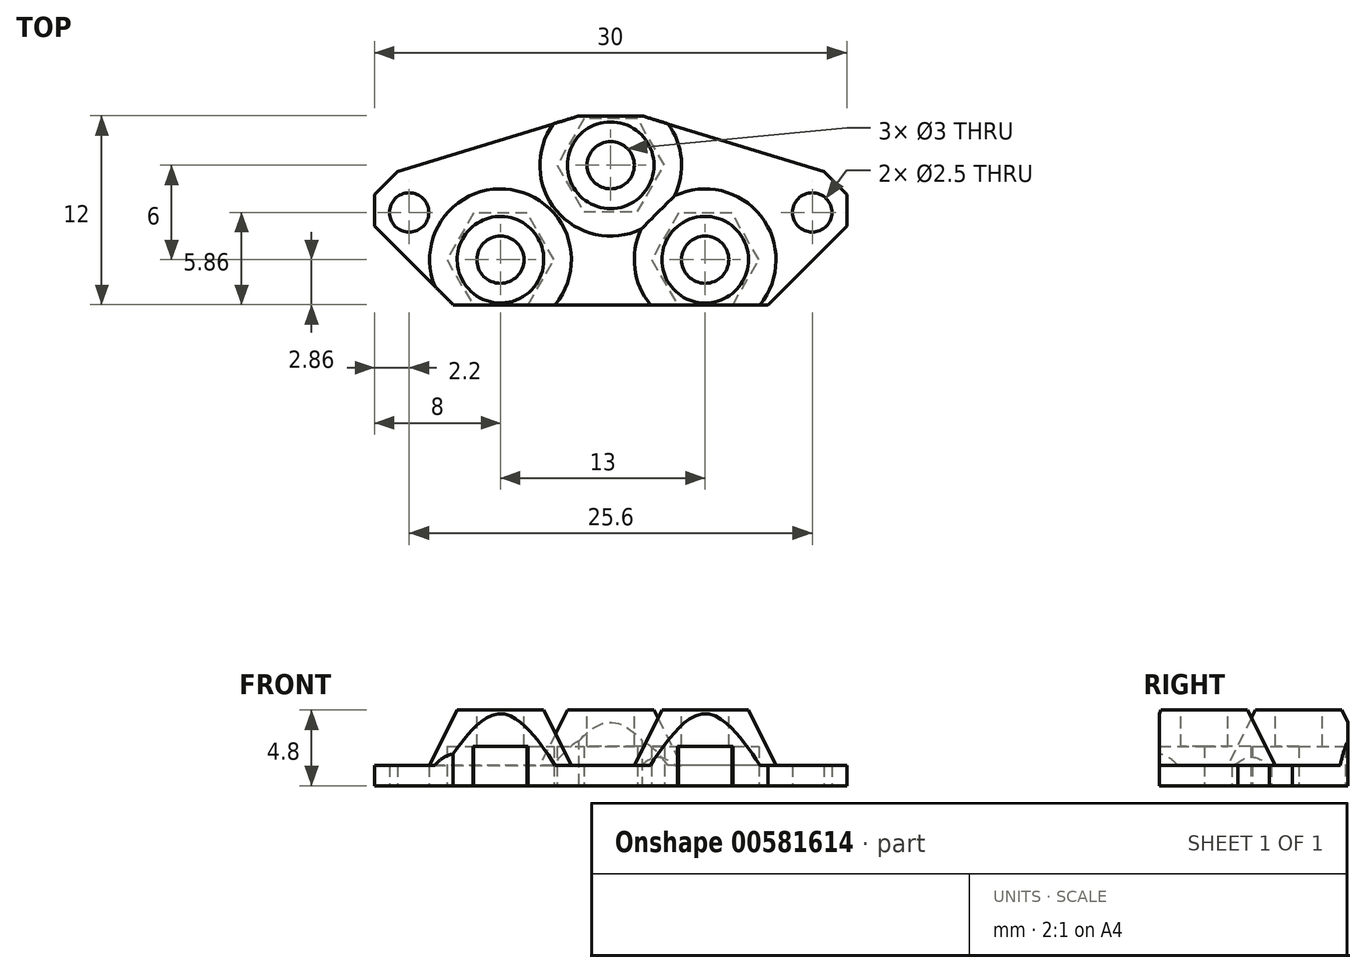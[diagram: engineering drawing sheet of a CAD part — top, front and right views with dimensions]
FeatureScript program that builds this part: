
annotation { "Feature Type Name" : "Feature", "Feature Type Description" : "" }
export const myFeature = defineFeature(function(context is Context, id is Id, definition is map)
    precondition{}
    {
        {
            var Q0;
            Q0=qCreatedBy(makeId("Top.planeOp"),FACE);
            var sketch = newSketch(context, id + "F0", { "sketchPlane" : qUnion([Q0])});
            skLineSegment(sketch, "E0.bottom", {"start": v(-15, 6.14) * mm, "end": v(15, 6.14) * mm});
            skLineSegment(sketch, "E0.top", {"start": v(-15, -5.86) * mm, "end": v(15, -5.86) * mm});
            skLineSegment(sketch, "E0.left", {"start": v(-15, 6.14) * mm, "end": v(-15, -5.86) * mm});
            skLineSegment(sketch, "E0.right", {"start": v(15, 6.14) * mm, "end": v(15, -5.86) * mm});
            skCircle(sketch, "E1", {"center": v(-12.8, 0) * mm, "radius": 1.25 * mm});
            skCircle(sketch, "E2", {"center": v(12.8, 0) * mm, "radius": 1.25 * mm});
            skSolve(sketch);
        }
        {
            var Q0;
            Q0=makeQuery(id+"F0.imprint","IMPRINT",FACE,{"disambiguationData":[TD([[makeQuery(id+"F0.imprint","IMPRINT",EDGE,{"derivedFrom":sQuery(id+"F0.wireOp",EDGE,"E0.bottom")}),-1.0]])]});
            extrude(context, id + "F1", {"entities" : qUnion([Q0]), "depth" : 4.8 * mm, "offsetDistance" : 25 * mm});
        }
        {
            var Q0;
            Q0=makeQuery(id+"F1.opExtrude","CAP_FACE",FACE,{"disambiguationData":[OSD([sQuery(id+"F0.wireOp",EDGE,"E0.bottom"),sQuery(id+"F0.wireOp",EDGE,"E0.top"),sQuery(id+"F0.wireOp",EDGE,"E0.left"),sQuery(id+"F0.wireOp",EDGE,"E0.right"),sQuery(id+"F0.wireOp",EDGE,"E1"),sQuery(id+"F0.wireOp",EDGE,"E2")])],"isStart":false});
            var sketch = newSketch(context, id + "F2", { "sketchPlane" : qUnion([Q0])});
            skCircle(sketch, "E3.0", {"center": v(-12.8, 0) * mm, "radius": 1.25 * mm, "construction": true});
            skCircle(sketch, "E4.0", {"center": v(12.8, 0) * mm, "radius": 1.25 * mm, "construction": true});
            skCircle(sketch, "E5", {"center": v(0, 3) * mm, "radius": 1.5 * mm});
            skCircle(sketch, "E6", {"center": v(-7, -3) * mm, "radius": 1.5 * mm});
            skCircle(sketch, "E7", {"center": v(6, -3) * mm, "radius": 1.5 * mm});
            skCircle(sketch, "E8", {"center": v(-7, -3) * mm, "radius": 2.5 * mm});
            skCircle(sketch, "E9", {"center": v(0, 3) * mm, "radius": 2.5 * mm});
            skCircle(sketch, "E10", {"center": v(6, -3) * mm, "radius": 2.5 * mm});
            skSolve(sketch);
        }
        {
            var Q0;
            Q0=makeQuery(id+"F1.opExtrude","CAP_FACE",FACE,{"disambiguationData":[OSD([sQuery(id+"F0.wireOp",EDGE,"E0.bottom"),sQuery(id+"F0.wireOp",EDGE,"E0.top"),sQuery(id+"F0.wireOp",EDGE,"E0.left"),sQuery(id+"F0.wireOp",EDGE,"E0.right"),sQuery(id+"F0.wireOp",EDGE,"E1"),sQuery(id+"F0.wireOp",EDGE,"E2")])],"isStart":true});
            var sketch = newSketch(context, id + "F3", { "sketchPlane" : qUnion([Q0])});
            skCircle(sketch, "E11.0", {"center": v(-7, 3) * mm, "radius": 2.5 * mm, "construction": true});
            skCircle(sketch, "E12.0", {"center": v(-7, 3) * mm, "radius": 1.5 * mm, "construction": true});
            skCircle(sketch, "E13.0", {"center": v(0, -3) * mm, "radius": 2.5 * mm, "construction": true});
            skCircle(sketch, "E14.0", {"center": v(0, -3) * mm, "radius": 1.5 * mm, "construction": true});
            skCircle(sketch, "E15.0", {"center": v(6, 3) * mm, "radius": 2.5 * mm, "construction": true});
            skCircle(sketch, "E16.0", {"center": v(6, 3) * mm, "radius": 1.5 * mm, "construction": true});
            skCircle(sketch, "E17.cCircle", {"center": v(-7, 3) * mm, "radius": 2.95 * mm, "construction": true});
            skLineSegment(sketch, "E17.0", {"start": v(-8.7, 5.95) * mm, "end": v(-5.3, 5.95) * mm});
            skLineSegment(sketch, "E17.1", {"start": v(-5.3, 5.95) * mm, "end": v(-3.6, 3) * mm});
            skLineSegment(sketch, "E17.2", {"start": v(-3.6, 3) * mm, "end": v(-5.3, 0.05) * mm});
            skLineSegment(sketch, "E17.3", {"start": v(-5.3, 0.05) * mm, "end": v(-8.7, 0.05) * mm});
            skLineSegment(sketch, "E17.4", {"start": v(-8.7, 0.05) * mm, "end": v(-10.4, 3) * mm});
            skLineSegment(sketch, "E17.5", {"start": v(-10.4, 3) * mm, "end": v(-8.7, 5.95) * mm});
            skPoint(sketch, "E17.0.midPoint", {"position": v(-7, 5.95) * mm});
            skCircle(sketch, "E18.cCircle", {"center": v(0, -3) * mm, "radius": 2.95 * mm, "construction": true});
            skLineSegment(sketch, "E18.0", {"start": v(1.7, -5.95) * mm, "end": v(-1.7, -5.95) * mm});
            skLineSegment(sketch, "E18.1", {"start": v(-1.7, -5.95) * mm, "end": v(-3.4, -3) * mm});
            skLineSegment(sketch, "E18.2", {"start": v(-3.4, -3) * mm, "end": v(-1.7, -0.05) * mm});
            skLineSegment(sketch, "E18.3", {"start": v(-1.7, -0.05) * mm, "end": v(1.7, -0.05) * mm});
            skLineSegment(sketch, "E18.4", {"start": v(1.7, -0.05) * mm, "end": v(3.4, -3) * mm});
            skLineSegment(sketch, "E18.5", {"start": v(3.4, -3) * mm, "end": v(1.7, -5.95) * mm});
            skPoint(sketch, "E18.0.midPoint", {"position": v(0, -5.95) * mm});
            skCircle(sketch, "E19.cCircle", {"center": v(6, 3) * mm, "radius": 2.95 * mm, "construction": true});
            skLineSegment(sketch, "E19.0", {"start": v(4.3, 5.95) * mm, "end": v(7.7, 5.95) * mm});
            skLineSegment(sketch, "E19.1", {"start": v(7.7, 5.95) * mm, "end": v(9.4, 3) * mm});
            skLineSegment(sketch, "E19.2", {"start": v(9.4, 3) * mm, "end": v(7.7, 0.05) * mm});
            skLineSegment(sketch, "E19.3", {"start": v(7.7, 0.05) * mm, "end": v(4.3, 0.05) * mm});
            skLineSegment(sketch, "E19.4", {"start": v(4.3, 0.05) * mm, "end": v(2.6, 3) * mm});
            skLineSegment(sketch, "E19.5", {"start": v(2.6, 3) * mm, "end": v(4.3, 5.95) * mm});
            skPoint(sketch, "E19.0.midPoint", {"position": v(6, 5.95) * mm});
            skSolve(sketch);
        }
        {
            var Q0;
            Q0=makeQuery(id+"F2.imprint","IMPRINT",FACE,{"disambiguationData":[TD([[makeQuery(id+"F2.imprint","IMPRINT",EDGE,{"derivedFrom":sQuery(id+"F2.wireOp",EDGE,"E6")}),1.0]])]});
            var Q1;
            Q1=makeQuery(id+"F2.imprint","IMPRINT",FACE,{"disambiguationData":[TD([[makeQuery(id+"F2.imprint","IMPRINT",EDGE,{"derivedFrom":sQuery(id+"F2.wireOp",EDGE,"E5")}),1.0]])]});
            var Q2;
            Q2=makeQuery(id+"F2.imprint","IMPRINT",FACE,{"disambiguationData":[TD([[makeQuery(id+"F2.imprint","IMPRINT",EDGE,{"derivedFrom":sQuery(id+"F2.wireOp",EDGE,"E7")}),1.0]])]});
            var Q3;
            Q3=sQuery(id+"F2.wireOp",EDGE,"E5");
            var Q4;
            Q4=sQuery(id+"F2.wireOp",EDGE,"E6");
            var Q5;
            Q5=sQuery(id+"F2.wireOp",EDGE,"E7");
            extrude(context, id + "F4", {"entities" : qUnion([Q0, Q1, Q2]), "operationType" : NewBodyOperationType.REMOVE, "surfaceEntities" : qUnion([Q3, Q4, Q5]), "endBound" : BoundingType.UP_TO_NEXT, "oppositeDirection" : true, "depth" : 25 * mm, "offsetDistance" : 25 * mm});
        }
        {
            var Q0;
            Q0=makeQuery(id+"F2.imprint","IMPRINT",FACE,{"disambiguationData":[TD([[makeQuery(id+"F2.imprint","IMPRINT",EDGE,{"derivedFrom":sQuery(id+"F2.wireOp",EDGE,"E8")}),-1.0]])]});
            extrude(context, id + "F5", {"entities" : qUnion([Q0]), "operationType" : NewBodyOperationType.REMOVE, "oppositeDirection" : true, "depth" : 3.5 * mm, "offsetDistance" : 25 * mm});
        }
        {
            var Q0;
            Q0=makeQuery(id+"F5.boolean.opBoolean","COPY",EDGE,{"derivedFrom":makeQuery(id+"F5.opExtrude","CAP_EDGE",EDGE,{"disambiguationData":[OSD([sQuery(id+"F2.wireOp",EDGE,"E8")])],"isStart":false})});
            var Q1;
            Q1=makeQuery(id+"F5.boolean.opBoolean","COPY",EDGE,{"derivedFrom":makeQuery(id+"F5.opExtrude","CAP_EDGE",EDGE,{"disambiguationData":[OSD([sQuery(id+"F2.wireOp",EDGE,"E9")])],"isStart":false})});
            var Q2;
            Q2=makeQuery(id+"F5.boolean.opBoolean","COPY",EDGE,{"derivedFrom":makeQuery(id+"F5.opExtrude","CAP_EDGE",EDGE,{"disambiguationData":[OSD([sQuery(id+"F2.wireOp",EDGE,"E10")])],"isStart":false})});
            chamfer(context, id + "F6", {"entities" : qUnion([Q0, Q1, Q2]), "chamferType" : ChamferType.TWO_OFFSETS, "width1" : 4 * mm, "oppositeDirection" : false, "width2" : 2 * mm, "tangentPropagation" : true});
        }
        {
            var Q0;
            Q0=makeQuery(id+"F3.imprint","IMPRINT",FACE,{"disambiguationData":[TD([[makeQuery(id+"F3.imprint","IMPRINT",EDGE,{"derivedFrom":sQuery(id+"F3.wireOp",EDGE,"E17.0")}),-1.0]])]});
            var Q1;
            {var subQ1=sQuery(id+"F3.wireOp",EDGE,"E19.2");Q1=makeQuery(id+"F3.imprint","IMPRINT",FACE,{"disambiguationData":[TD([[makeQuery(id+"F3.imprint","IMPRINT",EDGE,{"derivedFrom":subQ1}),-1.0]])]});}
            var Q2;
            Q2=makeQuery(id+"F3.imprint","IMPRINT",FACE,{"disambiguationData":[TD([[makeQuery(id+"F3.imprint","IMPRINT",EDGE,{"derivedFrom":sQuery(id+"F3.wireOp",EDGE,"E18.0")}),-1.0]])]});
            var Q3;
            {var subQ1=sQuery(id+"F3.wireOp",EDGE,"E17.2");Q3=makeQuery(id+"F3.imprint","IMPRINT",FACE,{"disambiguationData":[TD([[makeQuery(id+"F3.imprint","IMPRINT",EDGE,{"derivedFrom":subQ1}),-1.0]])]});}
            extrude(context, id + "F7", {"entities" : qUnion([Q0, Q1, Q2, Q3]), "operationType" : NewBodyOperationType.REMOVE, "oppositeDirection" : true, "depth" : 2.5 * mm, "offsetDistance" : 25 * mm});
        }
        {
            var Q0;
            Q0=makeQuery(id+"F1.opExtrude","SWEPT_EDGE",EDGE,{"disambiguationData":[OSD([sQuery(id+"F0.wireOp",EDGE,"E0.bottom"),sQuery(id+"F0.wireOp",EDGE,"E0.left")])]});
            var Q1;
            Q1=makeQuery(id+"F1.opExtrude","SWEPT_EDGE",EDGE,{"disambiguationData":[OSD([sQuery(id+"F0.wireOp",EDGE,"E0.top"),sQuery(id+"F0.wireOp",EDGE,"E0.left")])]});
            var Q2;
            Q2=makeQuery(id+"F1.opExtrude","SWEPT_EDGE",EDGE,{"disambiguationData":[OSD([sQuery(id+"F0.wireOp",EDGE,"E0.bottom"),sQuery(id+"F0.wireOp",EDGE,"E0.right")])]});
            var Q3;
            Q3=makeQuery(id+"F1.opExtrude","SWEPT_EDGE",EDGE,{"disambiguationData":[OSD([sQuery(id+"F0.wireOp",EDGE,"E0.top"),sQuery(id+"F0.wireOp",EDGE,"E0.right")])]});
            chamfer(context, id + "F8", {"entities" : qUnion([Q0, Q1, Q2, Q3]), "width" : 5 * mm, "tangentPropagation" : true});
        }
        {
            var Q0;
            {var subQ0=sQuery(id+"F0.wireOp",EDGE,"E0.bottom");Q0=makeQuery(id+"F8.opChamfer","BLEND_EDGE",EDGE,{"blendedFrom":[makeQuery(id+"F1.opExtrude","SWEPT_EDGE",EDGE,{"disambiguationData":[OSD([subQ0,sQuery(id+"F0.wireOp",EDGE,"E0.right")])]}),makeQuery(id+"F1.opExtrude","SWEPT_FACE",FACE,{"disambiguationData":[OSD([subQ0])]})],"blendedInto":[makeQuery(id+"F1.opExtrude","SWEPT_FACE",FACE,{"disambiguationData":[OSD([subQ0])]})]});}
            var Q1;
            {var subQ0=sQuery(id+"F0.wireOp",EDGE,"E0.bottom");Q1=makeQuery(id+"F8.opChamfer","BLEND_EDGE",EDGE,{"blendedFrom":[makeQuery(id+"F1.opExtrude","SWEPT_EDGE",EDGE,{"disambiguationData":[OSD([subQ0,sQuery(id+"F0.wireOp",EDGE,"E0.left")])]}),makeQuery(id+"F1.opExtrude","SWEPT_FACE",FACE,{"disambiguationData":[OSD([subQ0])]})],"blendedInto":[makeQuery(id+"F1.opExtrude","SWEPT_FACE",FACE,{"disambiguationData":[OSD([subQ0])]})]});}
            chamfer(context, id + "F9", {"entities" : qUnion([Q0, Q1]), "chamferType" : ChamferType.TWO_OFFSETS, "width1" : 8 * mm, "oppositeDirection" : false, "width2" : 5 * mm, "tangentPropagation" : true});
        }
    });
